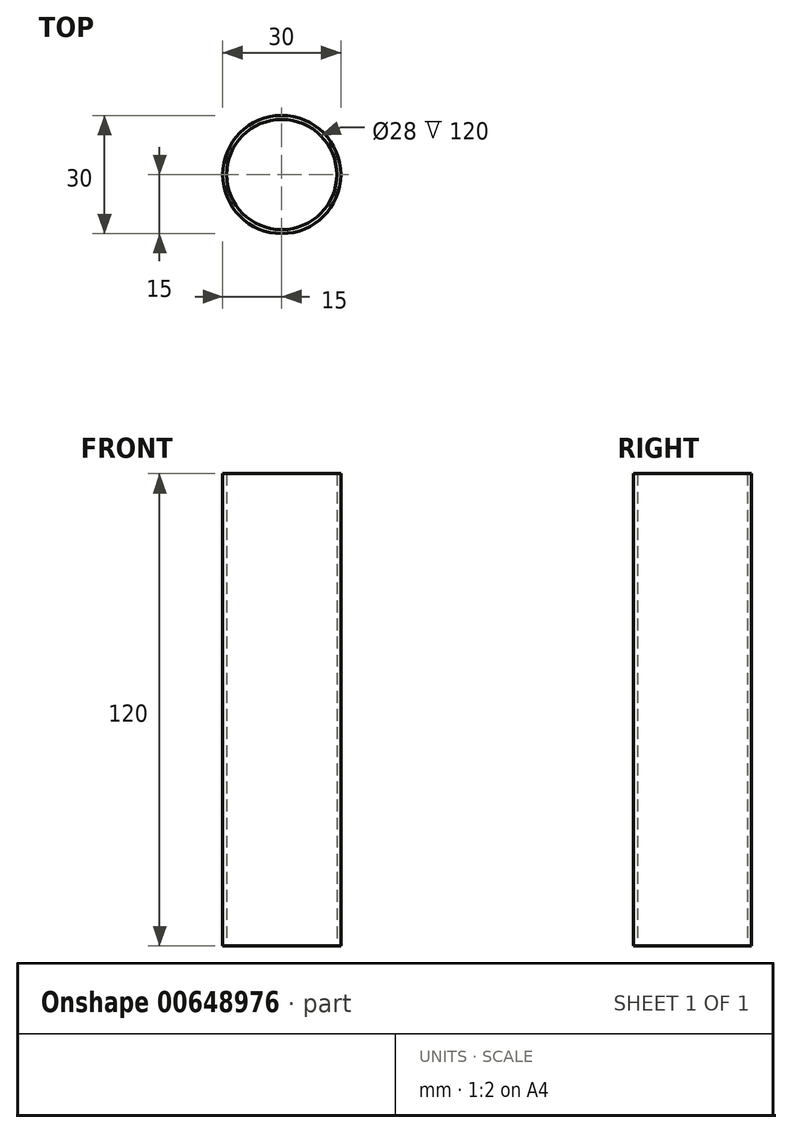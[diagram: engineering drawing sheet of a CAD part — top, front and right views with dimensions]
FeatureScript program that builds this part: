
annotation { "Feature Type Name" : "Feature", "Feature Type Description" : "" }
export const myFeature = defineFeature(function(context is Context, id is Id, definition is map)
    precondition{}
    {
        {
            var Q0;
            Q0=qCreatedBy(makeId("Top.planeOp"),FACE);
            var sketch = newSketch(context, id + "F0", { "sketchPlane" : qUnion([Q0])});
            skCircle(sketch, "E0", {"center": v(0, 0) * mm, "radius": 15 * mm});
            skCircle(sketch, "E1", {"center": v(0, 0) * mm, "radius": 14 * mm});
            skSolve(sketch);
        }
        {
            var Q0;
            Q0 = qSketchRegion(id + "F0", true);
            extrude(context, id + "F1", {"entities" : qUnion([Q0]), "depth" : 120 * mm, "offsetDistance" : 25 * mm});
        }
    });
